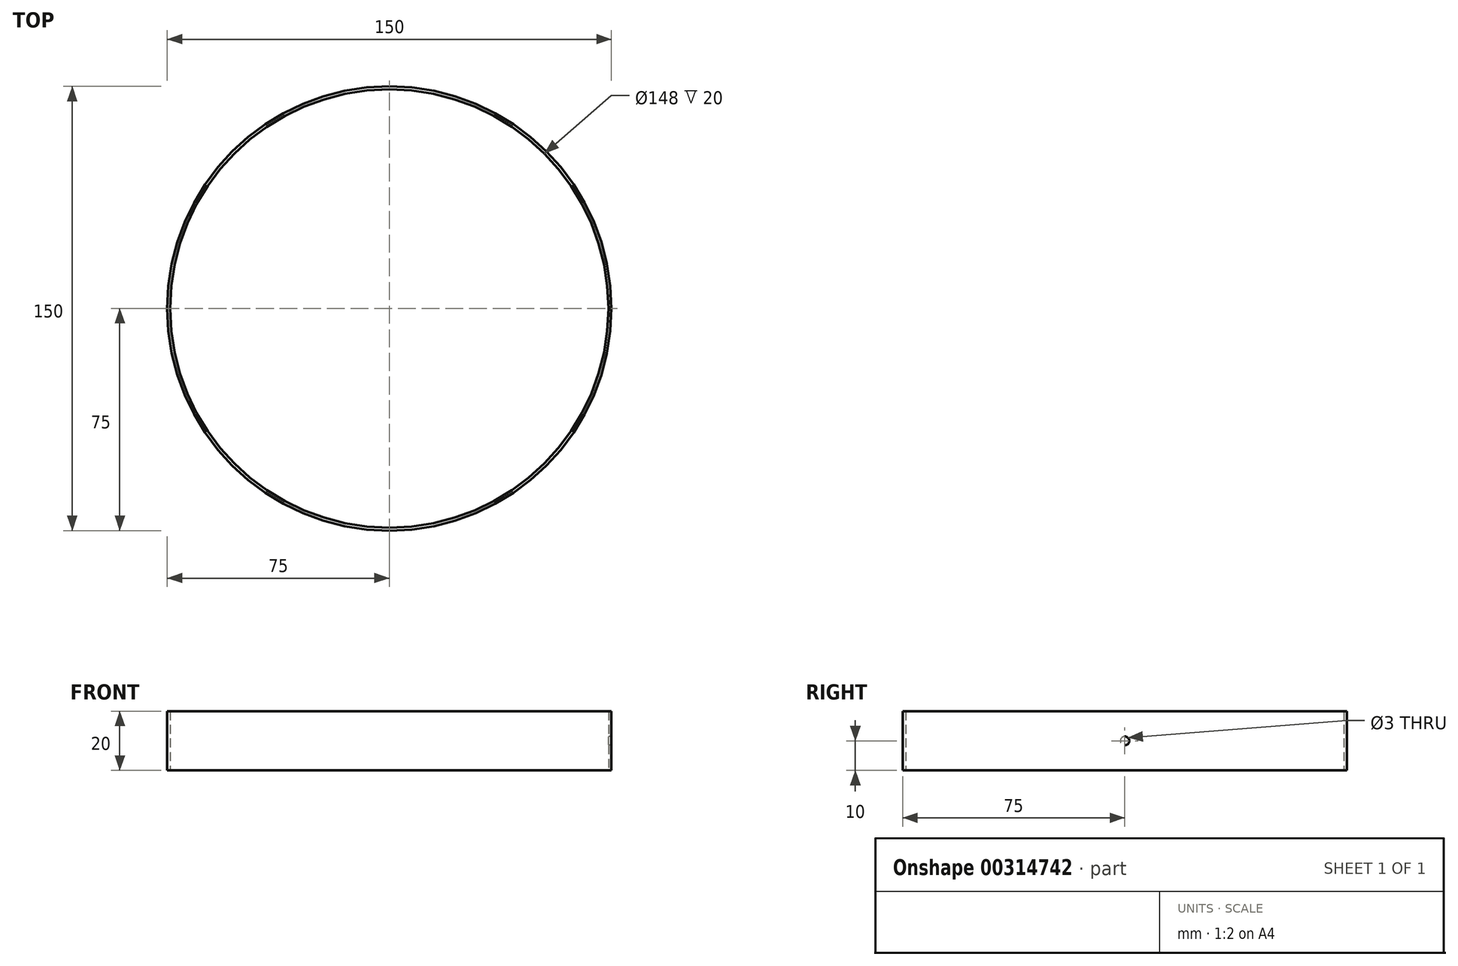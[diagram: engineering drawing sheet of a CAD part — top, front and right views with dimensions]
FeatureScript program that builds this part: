
annotation { "Feature Type Name" : "Feature", "Feature Type Description" : "" }
export const myFeature = defineFeature(function(context is Context, id is Id, definition is map)
    precondition{}
    {
        {
            var Q0;
            Q0=qCreatedBy(makeId("Top.planeOp"),FACE);
            var sketch = newSketch(context, id + "F0", { "sketchPlane" : qUnion([Q0])});
            skCircle(sketch, "E0", {"center": v(0, 0) * mm, "radius": 75 * mm});
            skCircle(sketch, "E1.0", {"center": v(0, 0) * mm, "radius": 74 * mm});
            skCircle(sketch, "E2.0", {"center": v(0, 0) * mm, "radius": 72 * mm});
            skCircle(sketch, "E3.0", {"center": v(0, 0) * mm, "radius": 71 * mm});
            skCircle(sketch, "E4.0", {"center": v(0, 0) * mm, "radius": 69 * mm});
            skCircle(sketch, "E5.0", {"center": v(0, 0) * mm, "radius": 68 * mm});
            skCircle(sketch, "E6.0", {"center": v(0, 0) * mm, "radius": 66 * mm});
            skCircle(sketch, "E7.0", {"center": v(0, 0) * mm, "radius": 65 * mm});
            skCircle(sketch, "E8.0", {"center": v(0, 0) * mm, "radius": 63 * mm});
            skCircle(sketch, "E9.0", {"center": v(0, 0) * mm, "radius": 62 * mm});
            skCircle(sketch, "E10.0", {"center": v(0, 0) * mm, "radius": 60 * mm});
            skCircle(sketch, "E11.0", {"center": v(0, 0) * mm, "radius": 59 * mm});
            skCircle(sketch, "E12.0", {"center": v(0, 0) * mm, "radius": 57 * mm});
            skCircle(sketch, "E13.0", {"center": v(0, 0) * mm, "radius": 56.05 * mm});
            skCircle(sketch, "E14.0", {"center": v(0, 0) * mm, "radius": 54.05 * mm});
            skCircle(sketch, "E15.0", {"center": v(0, 0) * mm, "radius": 53.05 * mm});
            skSolve(sketch);
        }
        {
            var Q0;
            Q0=makeQuery(id+"F0.imprint","IMPRINT",FACE,{"disambiguationData":[TD([[makeQuery(id+"F0.imprint","IMPRINT",EDGE,{"derivedFrom":sQuery(id+"F0.wireOp",EDGE,"E0")}),1.0]])]});
            extrude(context, id + "F1", {"entities" : qUnion([Q0]), "depth" : 20 * mm});
        }
        {
            var Q0;
            Q0=qCreatedBy(makeId("Right.planeOp"),FACE);
            var sketch = newSketch(context, id + "F2", { "sketchPlane" : qUnion([Q0])});
            skCircle(sketch, "E16", {"center": v(0, 10) * mm, "radius": 1.5 * mm});
            skSolve(sketch);
        }
        {
            var Q0;
            Q0=qSketchRegion(id+"F2",true);
            extrude(context, id + "F3", {"entities" : qUnion([Q0]), "operationType" : NewBodyOperationType.REMOVE, "endBound" : BoundingType.THROUGH_ALL, "depth" : 86.5 * mm});
        }
    });
